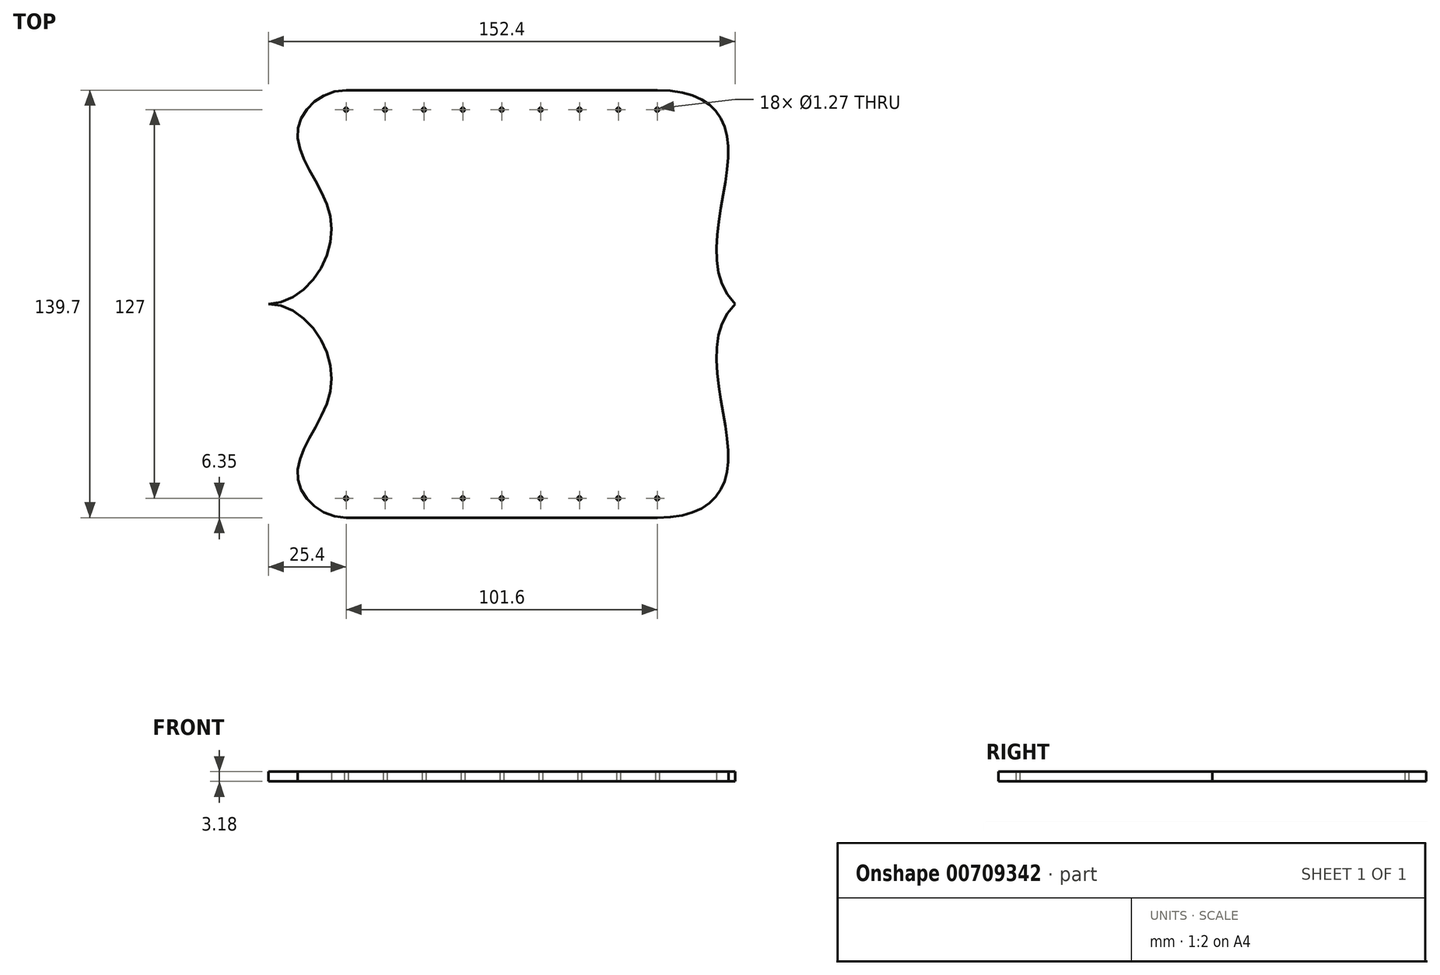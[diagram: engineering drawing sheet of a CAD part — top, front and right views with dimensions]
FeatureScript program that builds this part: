
annotation { "Feature Type Name" : "Feature", "Feature Type Description" : "" }
export const myFeature = defineFeature(function(context is Context, id is Id, definition is map)
    precondition{}
    {
        {
            var Q0;
            Q0=qCreatedBy(makeId("Top.planeOp"),FACE);
            var sketch = newSketch(context, id + "F0", { "sketchPlane" : qUnion([Q0])});
            skLineSegment(sketch, "E0", {"start": v(-76.2, 0) * mm, "end": v(76.2, 0) * mm, "construction": true});
            skLineSegment(sketch, "E1", {"start": v(-76.2, 0) * mm, "end": v(-76.2, 69.85) * mm, "construction": true});
            skLineSegment(sketch, "E2", {"start": v(76.2, 0) * mm, "end": v(76.2, 69.85) * mm, "construction": true});
            skLineSegment(sketch, "E3", {"start": v(-50.8, 69.85) * mm, "end": v(50.8, 69.85) * mm});
            skLineSegment(sketch, "E4", {"start": v(-76.2, 0) * mm, "end": v(-76.2, -25.41) * mm, "construction": true});
            skPoint(sketch, "E5", {"position": v(-38.1, 63.5) * mm});
            skPoint(sketch, "E6", {"position": v(-25.4, 63.5) * mm});
            skPoint(sketch, "E7", {"position": v(-12.7, 63.5) * mm});
            skPoint(sketch, "E8", {"position": v(0, 63.5) * mm});
            skPoint(sketch, "E9", {"position": v(12.7, 63.5) * mm});
            skPoint(sketch, "E10", {"position": v(25.4, 63.5) * mm});
            skPoint(sketch, "E11", {"position": v(38.1, 63.5) * mm});
            skPoint(sketch, "E12", {"position": v(50.8, 63.5) * mm});
            skPoint(sketch, "E13", {"position": v(-50.8, 63.5) * mm});
            skFitSpline(sketch, "E14", {"points": [v(-50.8, 69.85) * mm, v(-66.68, 55.25) * mm, v(-55.56, 25.4) * mm, v(-76.2, 0) * mm], "startDerivative": vector(-90.97, 0) * mm, "endDerivative": vector(-97.6, 0) * mm});
            skFitSpline(sketch, "E15", {"points": [v(50.8, 69.85) * mm, v(73.98, 52.07) * mm, v(76.2, 0) * mm], "startDerivative": vector(103.27, 0) * mm, "endDerivative": vector(66.62, -66.62) * mm});
            skCircle(sketch, "E16", {"center": v(-50.8, 63.5) * mm, "radius": 0.64 * mm});
            skCircle(sketch, "E17", {"center": v(-38.1, 63.5) * mm, "radius": 0.64 * mm});
            skCircle(sketch, "E18", {"center": v(-25.4, 63.5) * mm, "radius": 0.64 * mm});
            skCircle(sketch, "E19", {"center": v(-12.7, 63.5) * mm, "radius": 0.64 * mm});
            skCircle(sketch, "E20", {"center": v(0, 63.5) * mm, "radius": 0.64 * mm});
            skCircle(sketch, "E21", {"center": v(12.7, 63.5) * mm, "radius": 0.64 * mm});
            skCircle(sketch, "E22", {"center": v(25.4, 63.5) * mm, "radius": 0.64 * mm});
            skCircle(sketch, "E23", {"center": v(38.1, 63.5) * mm, "radius": 0.64 * mm});
            skCircle(sketch, "E24", {"center": v(50.8, 63.5) * mm, "radius": 0.64 * mm});
            skCircle(sketch, "E25.MirrorC", {"center": v(-12.7, -63.5) * mm, "radius": 0.64 * mm});
            skCircle(sketch, "E26.MirrorC", {"center": v(50.8, -63.5) * mm, "radius": 0.64 * mm});
            skCircle(sketch, "E27.MirrorC", {"center": v(-50.8, -63.5) * mm, "radius": 0.64 * mm});
            skCircle(sketch, "E28.MirrorC", {"center": v(12.7, -63.5) * mm, "radius": 0.64 * mm});
            skCircle(sketch, "E29.MirrorC", {"center": v(0, -63.5) * mm, "radius": 0.64 * mm});
            skCircle(sketch, "E30.MirrorC", {"center": v(25.4, -63.5) * mm, "radius": 0.64 * mm});
            skCircle(sketch, "E31.MirrorC", {"center": v(-38.1, -63.5) * mm, "radius": 0.64 * mm});
            skCircle(sketch, "E32.MirrorC", {"center": v(-25.4, -63.5) * mm, "radius": 0.64 * mm});
            skCircle(sketch, "E33.MirrorC", {"center": v(38.1, -63.5) * mm, "radius": 0.64 * mm});
            skLineSegment(sketch, "E34.MirrorCS", {"start": v(-76.2, 0) * mm, "end": v(-76.2, -69.85) * mm, "construction": true});
            skFitSpline(sketch, "E35.MirrorCS", {"points": [v(50.8, -69.85) * mm, v(73.98, -52.07) * mm, v(76.2, 0) * mm], "startDerivative": vector(103.27, 0) * mm, "endDerivative": vector(66.62, 66.62) * mm});
            skFitSpline(sketch, "E36.MirrorCS", {"points": [v(-50.8, -69.85) * mm, v(-66.68, -55.25) * mm, v(-55.56, -25.4) * mm, v(-76.2, 0) * mm], "startDerivative": vector(-90.97, 0) * mm, "endDerivative": vector(-97.6, 0) * mm});
            skLineSegment(sketch, "E37.MirrorCS", {"start": v(-50.8, -69.85) * mm, "end": v(50.8, -69.85) * mm});
            skLineSegment(sketch, "E38.MirrorCS", {"start": v(76.2, 0) * mm, "end": v(76.2, -69.85) * mm, "construction": true});
            skLineSegment(sketch, "E39.MirrorCS", {"start": v(-76.2, 0) * mm, "end": v(-76.2, 25.41) * mm, "construction": true});
            skSolve(sketch);
        }
        {
            var Q0;
            Q0=makeQuery(id+"F0.imprint","IMPRINT",FACE,{"disambiguationData":[TD([[makeQuery(id+"F0.imprint","IMPRINT",EDGE,{"derivedFrom":sQuery(id+"F0.wireOp",EDGE,"E3")}),-1.0]])]});
            extrude(context, id + "F1", {"entities" : qUnion([Q0]), "depth" : 3.17 * mm, "offsetDistance" : 25.4 * mm});
        }
    });
